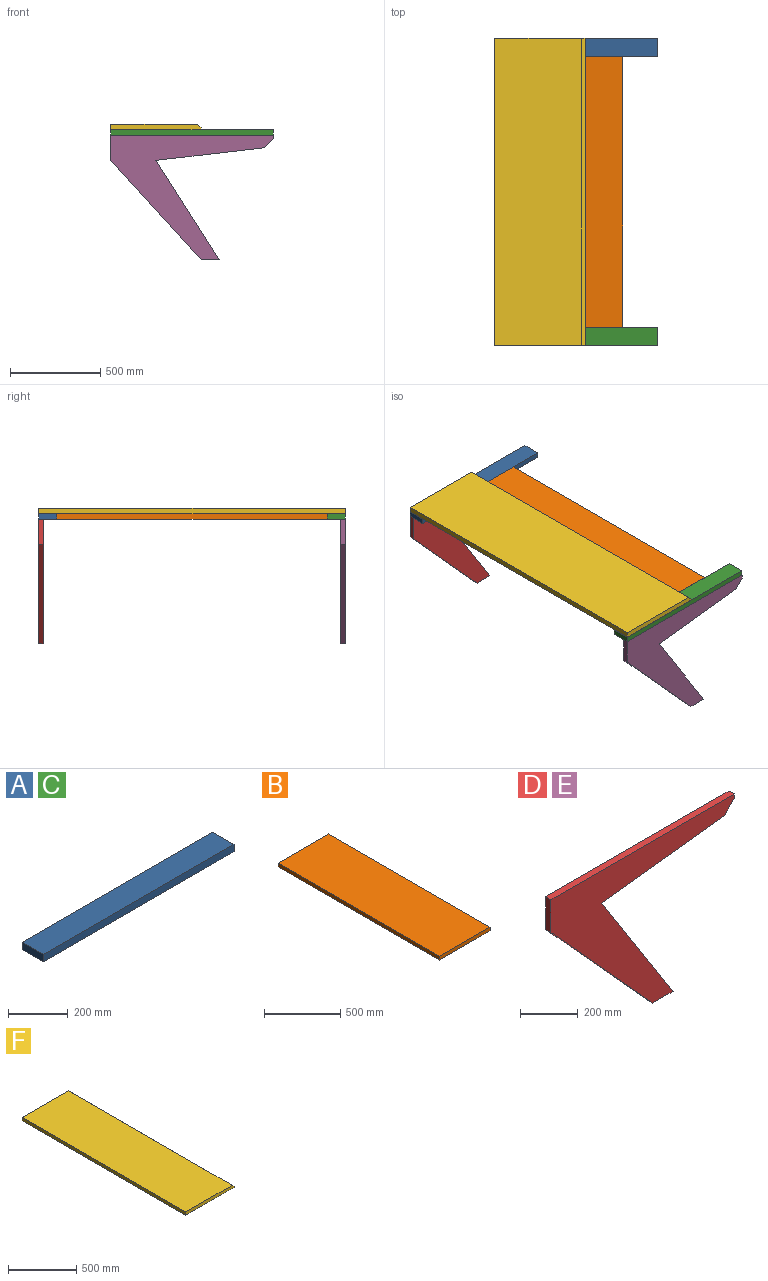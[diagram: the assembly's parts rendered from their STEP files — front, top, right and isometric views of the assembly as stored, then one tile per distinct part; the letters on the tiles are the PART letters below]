
ASSEMBLY  parts=6 mates=17
PART A: 6 faces, bbox 900x100x30 mm
  f0: plane 100x30mm, normal (-1,0,0), area 3000mm2, adj f1,f3,f4,f5
  f1: plane 900x100mm, normal (0,0,-1), area 90000mm2, adj f0,f2,f4,f5
  f2: plane 100x30mm, normal (1,0,0), area 3000mm2, adj f1,f3,f4,f5
  f3: plane 900x100mm, normal (0,0,1), area 90000mm2, adj f0,f2,f4,f5
  f4: plane 900x30mm, normal (0,1,0), area 27000mm2, adj f0,f1,f2,f3
  f5: plane 900x30mm, normal (0,-1,0), area 27000mm2, adj f0,f1,f2,f3
PART B: 6 faces, bbox 470x1500x30 mm
  f0: plane 1500x30mm, normal (1,0,0), area 45000mm2, adj f1,f3,f4,f5
  f1: plane 1500x470mm, normal (0,0,1), area 705000mm2, adj f0,f2,f4,f5
  f2: plane 1500x30mm, normal (-1,0,0), area 45000mm2, adj f1,f3,f4,f5
  f3: plane 1500x470mm, normal (0,0,-1), area 705000mm2, adj f0,f2,f4,f5
  f4: plane 470x30mm, normal (0,1,0), area 14100mm2, adj f0,f1,f2,f3
  f5: plane 470x30mm, normal (0,-1,0), area 14100mm2, adj f0,f1,f2,f3
PART C: same geometry as A
PART D: 10 faces, bbox 900x25x690 mm
  f0: plane 50x50mm, normal (0.71,0,-0.71), area 1767.8mm2, adj f1,f7,f8,f9
  f1: plane 25x20mm, normal (1,0,0), area 500mm2, adj f0,f2,f8,f9
  f2: plane 900x25mm, normal (0,0,1), area 22500mm2, adj f1,f3,f8,f9
  f3: plane 140x25mm, normal (-1,0,0), area 3500mm2, adj f2,f4,f8,f9
  f4: plane 550x500mm, normal (-0.74,0,-0.67), area 18582.6mm2, adj f3,f5,f8,f9
  f5: plane 100x25mm, normal (0,0,-1), area 2500mm2, adj f4,f6,f8,f9
  f6: plane 550x350mm, normal (0.84,0,0.54), area 16298mm2, adj f5,f7,f8,f9
  f7: plane 600x70mm, normal (0.12,0,-0.99), area 15101.7mm2, adj f0,f6,f8,f9
  f8: plane 900x690mm, normal (0,-1,0), area 196500mm2, adj f0,f1,f2,f3,f4,f5,f6,f7
  f9: plane 900x690mm, normal (0,1,0), area 196500mm2, adj f0,f1,f2,f3,f4,f5,f6,f7
PART E: same geometry as D
PART F: 7 faces, bbox 500x1700x30 mm
  f0: plane 1700x30mm, normal (-1,0,0), area 51000mm2, adj f1,f4,f5,f6
  f1: plane 1700x500mm, normal (0,0,-1), area 850000mm2, adj f0,f2,f5,f6
  f2: plane 1700x10mm, normal (1,0,0), area 17000mm2, adj f1,f3,f5,f6
  f3: plane 1700x20mm, normal (0.71,0,0.71), area 48083.3mm2, adj f2,f4,f5,f6
  f4: plane 1700x480mm, normal (0,0,1), area 816000mm2, adj f0,f3,f5,f6
  f5: plane 500x30mm, normal (0,1,0), area 14800mm2, adj f0,f1,f2,f3,f4
  f6: plane 500x30mm, normal (0,-1,0), area 14800mm2, adj f0,f1,f2,f3,f4
PLACE A t=(-356.99,954.16,310.16)mm
PLACE B t=(352.88,-545.84,340.16)mm
PLACE C t=(-356.99,-645.84,310.16)mm fixed
PLACE D t=(0,1700,-30)mm
PLACE E t=(0,25,-30)mm
PLACE F t=(-356.99,-645.84,370.16)mm
MATE planar A.f2 <-> C.f2  axis (1,0,0) through (543.01,1004.16,325.16)mm
MATE planar D.f1 <-> A.f2  axis (1,0,0) through (543.01,1041.66,300.16)mm
MATE planar F.f0 <-> C.f0  axis (-1,0,0) through (-356.99,-645.84,355.16)mm
MATE planar C.f3 <-> F.f1  axis (0,0,1) through (93.01,-595.84,340.16)mm
MATE planar C.f3 <-> B.f1  axis (0,0,1) through (93.01,-595.84,340.16)mm
MATE planar E.f8 <-> C.f5  axis (0,-1,0) through (-8.66,-645.84,95.92)mm
MATE planar D.f2 <-> A.f1  axis (0,0,1) through (93.01,1041.66,310.16)mm
MATE parallel B.f0 <-> C.f0  axis (1,0,0) through (352.88,204.16,325.16)mm
MATE planar B.f5 <-> C.f4  axis (0,-1,0) through (117.88,-545.84,325.16)mm
MATE planar A.f3 <-> C.f3  axis (0,0,1) through (93.01,1004.16,340.16)mm
MATE planar A.f5 <-> B.f4  axis (0,-1,0) through (93.01,954.16,325.16)mm
MATE planar F.f6 <-> C.f5  axis (0,-1,0) through (-110.28,-645.84,355.05)mm
MATE planar E.f2 <-> C.f1  axis (0,0,1) through (93.01,-633.34,310.16)mm
MATE planar A.f4 <-> D.f9  axis (0,1,0) through (93.01,1054.16,325.16)mm
MATE parallel F.f0 <-> C.f2  axis (-1,0,0) through (-356.99,204.16,355.16)mm
MATE parallel F.f4 <-> B.f1  axis (0,0,1) through (-116.99,204.16,370.16)mm
MATE planar E.f3 <-> C.f0  axis (-1,0,0) through (-356.99,-633.34,240.16)mm
